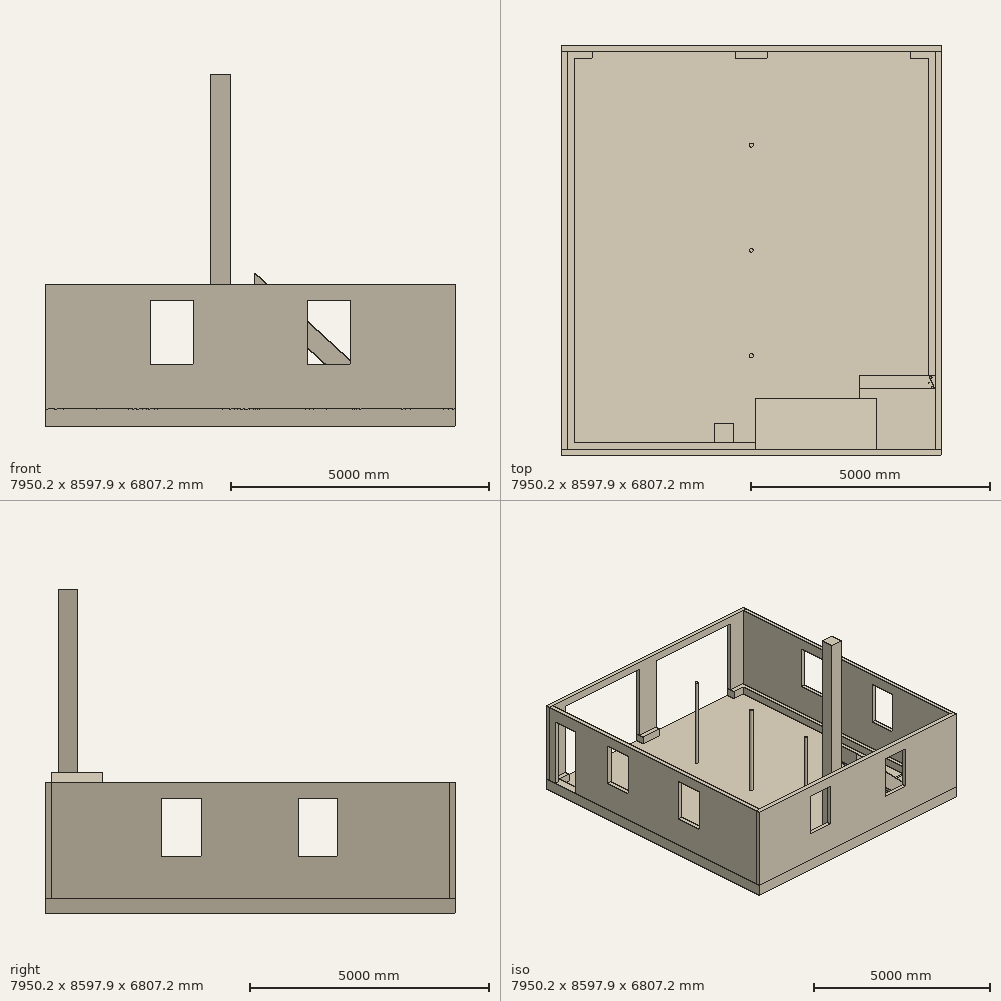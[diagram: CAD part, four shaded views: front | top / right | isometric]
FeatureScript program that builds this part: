
annotation { "Feature Type Name" : "Feature", "Feature Type Description" : "" }
export const myFeature = defineFeature(function(context is Context, id is Id, definition is map)
    precondition{}
    {
        {
            var Q0;
            Q0=qCreatedBy(makeId("Top.planeOp"),FACE);
            var sketch = newSketch(context, id + "F0", { "sketchPlane" : qUnion([Q0])});
            skLineSegment(sketch, "E0.rect.bottom", {"start": v(3975.1, 4298.95) * mm, "end": v(-3975.1, 4298.95) * mm});
            skLineSegment(sketch, "E0.rect.top", {"start": v(3975.1, -4298.95) * mm, "end": v(-3975.1, -4298.95) * mm});
            skLineSegment(sketch, "E0.rect.left", {"start": v(3975.1, 4298.95) * mm, "end": v(3975.1, -4298.95) * mm});
            skLineSegment(sketch, "E0.rect.right", {"start": v(-3975.1, 4298.95) * mm, "end": v(-3975.1, -4298.95) * mm});
            skPoint(sketch, "E0.rect.middle", {"position": v(0, 0) * mm});
            skSolve(sketch);
        }
        {
            var Q0;
            Q0 = qSketchRegion(id + "F0", true);
            extrude(context, id + "F1", {"entities" : qUnion([Q0]), "oppositeDirection" : true, "depth" : 101.6 * mm});
        }
        {
            var Q0;
            Q0=makeQuery(id+"F1.opExtrude","CAP_FACE",FACE,{"disambiguationData":[OSD([sQuery(id+"F0.wireOp",EDGE,"E0.rect.bottom"),sQuery(id+"F0.wireOp",EDGE,"E0.rect.top"),sQuery(id+"F0.wireOp",EDGE,"E0.rect.left"),sQuery(id+"F0.wireOp",EDGE,"E0.rect.right")])],"isStart":true});
            var sketch = newSketch(context, id + "F2", { "sketchPlane" : qUnion([Q0])});
            skLineSegment(sketch, "E1", {"start": v(-3327.4, 4298.95) * mm, "end": v(-3975.1, 4298.95) * mm});
            skLineSegment(sketch, "E2", {"start": v(-3975.1, 4298.95) * mm, "end": v(-3975.1, -4298.95) * mm});
            skLineSegment(sketch, "E3", {"start": v(-3975.1, -4298.95) * mm, "end": v(3975.1, -4298.95) * mm});
            skLineSegment(sketch, "E4", {"start": v(3975.1, -4298.95) * mm, "end": v(3975.1, 4298.95) * mm});
            skLineSegment(sketch, "E5", {"start": v(3975.1, 4298.95) * mm, "end": v(3327.4, 4298.95) * mm});
            skLineSegment(sketch, "E6.0", {"start": v(3708.4, 4032.25) * mm, "end": v(3327.4, 4032.25) * mm});
            skLineSegment(sketch, "E6.1", {"start": v(-3327.4, 4032.25) * mm, "end": v(-3708.4, 4032.25) * mm});
            skLineSegment(sketch, "E6.2", {"start": v(-3708.4, 4032.25) * mm, "end": v(-3708.4, -4032.25) * mm});
            skLineSegment(sketch, "E6.3", {"start": v(-3708.4, -4032.25) * mm, "end": v(3708.4, -4032.25) * mm});
            skLineSegment(sketch, "E6.4", {"start": v(3708.4, -4032.25) * mm, "end": v(3708.4, 4032.25) * mm});
            skLineSegment(sketch, "E7", {"start": v(-3327.4, 4298.95) * mm, "end": v(-3327.4, 4032.25) * mm});
            skLineSegment(sketch, "E8", {"start": v(-330.2, 4298.95) * mm, "end": v(-330.2, 4032.25) * mm});
            skLineSegment(sketch, "E9", {"start": v(-330.2, 4032.25) * mm, "end": v(330.2, 4032.25) * mm});
            skLineSegment(sketch, "E10", {"start": v(330.2, 4032.25) * mm, "end": v(330.2, 4298.95) * mm});
            skLineSegment(sketch, "E11", {"start": v(330.2, 4298.95) * mm, "end": v(-330.2, 4298.95) * mm});
            skLineSegment(sketch, "E12", {"start": v(-330.2, 4032.25) * mm, "end": v(-3327.4, 4032.25) * mm, "construction": true});
            skLineSegment(sketch, "E13", {"start": v(330.2, 4032.25) * mm, "end": v(3327.4, 4032.25) * mm, "construction": true});
            skLineSegment(sketch, "E14", {"start": v(3327.4, 4032.25) * mm, "end": v(3327.4, 4298.95) * mm});
            skSolve(sketch);
        }
        {
            var Q0;
            Q0 = qSketchRegion(id + "F2", true);
            extrude(context, id + "F3", {"entities" : qUnion([Q0]), "operationType" : NewBodyOperationType.ADD, "depth" : 228.6 * mm});
        }
        {
            var Q0;
            Q0=makeQuery(id+"F3.boolean.opBoolean","MERGE",FACE,{"derivedFrom":[makeQuery(id+"F1.opExtrude","SWEPT_FACE",FACE,{"disambiguationData":[OSD([sQuery(id+"F0.wireOp",EDGE,"E0.rect.bottom")])]}),makeQuery(id+"F3.opExtrude","SWEPT_FACE",FACE,{"disambiguationData":[OSD([sQuery(id+"F2.wireOp",EDGE,"E1")])]}),makeQuery(id+"F3.opExtrude","SWEPT_FACE",FACE,{"disambiguationData":[OSD([sQuery(id+"F2.wireOp",EDGE,"E5")])]}),makeQuery(id+"F3.opExtrude","SWEPT_FACE",FACE,{"disambiguationData":[OSD([sQuery(id+"F2.wireOp",EDGE,"E11")])]})]});
            var sketch = newSketch(context, id + "F4", { "sketchPlane" : qUnion([Q0])});
            skLineSegment(sketch, "E15", {"start": v(-3975.1, 228.6) * mm, "end": v(-3975.1, 2641.6) * mm});
            skLineSegment(sketch, "E16", {"start": v(-3975.1, 2641.6) * mm, "end": v(3975.1, 2641.6) * mm});
            skLineSegment(sketch, "E17", {"start": v(3975.1, 2641.6) * mm, "end": v(3975.1, 228.6) * mm});
            skLineSegment(sketch, "E18", {"start": v(3975.1, 228.6) * mm, "end": v(3327.4, 228.6) * mm});
            skLineSegment(sketch, "E19", {"start": v(3327.4, 228.6) * mm, "end": v(3327.4, 2413) * mm});
            skLineSegment(sketch, "E20", {"start": v(3327.4, 2413) * mm, "end": v(330.2, 2413) * mm});
            skLineSegment(sketch, "E21", {"start": v(330.2, 2413) * mm, "end": v(330.2, 228.6) * mm});
            skLineSegment(sketch, "E22", {"start": v(330.2, 228.6) * mm, "end": v(-330.2, 228.6) * mm});
            skLineSegment(sketch, "E23", {"start": v(-330.2, 228.6) * mm, "end": v(-330.2, 2413) * mm});
            skLineSegment(sketch, "E24", {"start": v(-330.2, 2413) * mm, "end": v(-3327.4, 2413) * mm});
            skLineSegment(sketch, "E25", {"start": v(-3327.4, 2413) * mm, "end": v(-3327.4, 228.6) * mm});
            skLineSegment(sketch, "E26", {"start": v(-3327.4, 228.6) * mm, "end": v(-3975.1, 228.6) * mm});
            skSolve(sketch);
        }
        {
            var Q0;
            Q0=makeQuery(id+"F4.imprint","IMPRINT",FACE,{"disambiguationData":[TD([[makeQuery(id+"F4.imprint","IMPRINT",EDGE,{"derivedFrom":sQuery(id+"F4.wireOp",EDGE,"E15")}),-1.0]])]});
            extrude(context, id + "F5", {"entities" : qUnion([Q0]), "oppositeDirection" : true, "depth" : 127 * mm});
        }
        {
            var Q0;
            Q0=makeQuery(id+"F3.boolean.opBoolean","MERGE",FACE,{"derivedFrom":[makeQuery(id+"F1.opExtrude","SWEPT_FACE",FACE,{"disambiguationData":[OSD([sQuery(id+"F0.wireOp",EDGE,"E0.rect.top")])]}),makeQuery(id+"F3.opExtrude","SWEPT_FACE",FACE,{"disambiguationData":[OSD([sQuery(id+"F2.wireOp",EDGE,"E3")])]})]});
            var sketch = newSketch(context, id + "F6", { "sketchPlane" : qUnion([Q0])});
            skLineSegment(sketch, "E27.bottom", {"start": v(-3975.1, 228.6) * mm, "end": v(3975.1, 228.6) * mm});
            skLineSegment(sketch, "E27.top", {"start": v(-3975.1, 2641.6) * mm, "end": v(3975.1, 2641.6) * mm});
            skLineSegment(sketch, "E27.left", {"start": v(-3975.1, 228.6) * mm, "end": v(-3975.1, 2641.6) * mm});
            skLineSegment(sketch, "E27.right", {"start": v(3975.1, 228.6) * mm, "end": v(3975.1, 2641.6) * mm});
            skLineSegment(sketch, "E28.bottom", {"start": v(-1930.4, 2324.1) * mm, "end": v(-1104.9, 2324.1) * mm});
            skLineSegment(sketch, "E28.top", {"start": v(-1930.4, 1092.2) * mm, "end": v(-1104.9, 1092.2) * mm});
            skLineSegment(sketch, "E28.left", {"start": v(-1930.4, 2324.1) * mm, "end": v(-1930.4, 1092.2) * mm});
            skLineSegment(sketch, "E28.right", {"start": v(-1104.9, 2324.1) * mm, "end": v(-1104.9, 1092.2) * mm});
            skLineSegment(sketch, "E29.bottom", {"start": v(1104.9, 2324.1) * mm, "end": v(1930.4, 2324.1) * mm});
            skLineSegment(sketch, "E29.top", {"start": v(1104.9, 1092.2) * mm, "end": v(1930.4, 1092.2) * mm});
            skLineSegment(sketch, "E29.left", {"start": v(1104.9, 2324.1) * mm, "end": v(1104.9, 1092.2) * mm});
            skLineSegment(sketch, "E29.right", {"start": v(1930.4, 2324.1) * mm, "end": v(1930.4, 1092.2) * mm});
            skLineSegment(sketch, "E30", {"start": v(0, 2641.6) * mm, "end": v(0, 228.6) * mm, "construction": true});
            skSolve(sketch);
        }
        {
            var Q0;
            Q0 = qSketchRegion(id + "F6", true);
            extrude(context, id + "F7", {"entities" : qUnion([Q0]), "oppositeDirection" : true, "depth" : 127 * mm});
        }
        {
            var Q0;
            Q0=makeQuery(id+"F3.boolean.opBoolean","MERGE",FACE,{"derivedFrom":[makeQuery(id+"F1.opExtrude","SWEPT_FACE",FACE,{"disambiguationData":[OSD([sQuery(id+"F0.wireOp",EDGE,"E0.rect.right")])]}),makeQuery(id+"F3.opExtrude","SWEPT_FACE",FACE,{"disambiguationData":[OSD([sQuery(id+"F2.wireOp",EDGE,"E2")])]})]});
            var sketch = newSketch(context, id + "F8", { "sketchPlane" : qUnion([Q0])});
            skLineSegment(sketch, "E31.top", {"start": v(-4171.95, 2641.6) * mm, "end": v(4171.95, 2641.6) * mm});
            skLineSegment(sketch, "E31.left", {"start": v(-4171.95, 228.6) * mm, "end": v(-4171.95, 2641.6) * mm});
            skLineSegment(sketch, "E31.right", {"start": v(4171.95, 228.6) * mm, "end": v(4171.95, 2641.6) * mm});
            skLineSegment(sketch, "E32", {"start": v(-4171.95, 228.6) * mm, "end": v(-3930.65, 228.6) * mm});
            skLineSegment(sketch, "E33", {"start": v(-3930.65, 228.6) * mm, "end": v(-3930.65, 2260.6) * mm});
            skLineSegment(sketch, "E34", {"start": v(-3930.65, 2260.6) * mm, "end": v(-3117.85, 2260.6) * mm});
            skLineSegment(sketch, "E35", {"start": v(-3117.85, 2260.6) * mm, "end": v(-3117.85, 228.6) * mm});
            skLineSegment(sketch, "E36", {"start": v(-3117.85, 228.6) * mm, "end": v(4171.95, 228.6) * mm});
            skLineSegment(sketch, "E37.bottom", {"start": v(-1822.45, 2324.1) * mm, "end": v(-996.95, 2324.1) * mm});
            skLineSegment(sketch, "E37.top", {"start": v(-1822.45, 1092.2) * mm, "end": v(-996.95, 1092.2) * mm});
            skLineSegment(sketch, "E37.left", {"start": v(-1822.45, 2324.1) * mm, "end": v(-1822.45, 1092.2) * mm});
            skLineSegment(sketch, "E37.right", {"start": v(-996.95, 2324.1) * mm, "end": v(-996.95, 1092.2) * mm});
            skLineSegment(sketch, "E38.bottom", {"start": v(1035.05, 2324.1) * mm, "end": v(1860.55, 2324.1) * mm});
            skLineSegment(sketch, "E38.top", {"start": v(1035.05, 1092.2) * mm, "end": v(1860.55, 1092.2) * mm});
            skLineSegment(sketch, "E38.left", {"start": v(1035.05, 2324.1) * mm, "end": v(1035.05, 1092.2) * mm});
            skLineSegment(sketch, "E38.right", {"start": v(1860.55, 2324.1) * mm, "end": v(1860.55, 1092.2) * mm});
            skSolve(sketch);
        }
        {
            var Q0;
            Q0=makeQuery(id+"F8.imprint","IMPRINT",FACE,{"disambiguationData":[TD([[makeQuery(id+"F8.imprint","IMPRINT",EDGE,{"derivedFrom":sQuery(id+"F8.wireOp",EDGE,"E31.bottom")}),1.0]])]});
            var Q1;
            Q1=makeQuery(id+"F8.imprint","IMPRINT",FACE,{"disambiguationData":[TD([[makeQuery(id+"F8.imprint","IMPRINT",EDGE,{"derivedFrom":sQuery(id+"F8.wireOp",EDGE,"E31.top")}),-1.0]])]});
            extrude(context, id + "F9", {"entities" : qUnion([Q0, Q1]), "oppositeDirection" : true, "depth" : 127 * mm});
        }
        {
            var Q0;
            Q0=makeQuery(id+"F3.boolean.opBoolean","MERGE",FACE,{"derivedFrom":[makeQuery(id+"F1.opExtrude","SWEPT_FACE",FACE,{"disambiguationData":[OSD([sQuery(id+"F0.wireOp",EDGE,"E0.rect.left")])]}),makeQuery(id+"F3.opExtrude","SWEPT_FACE",FACE,{"disambiguationData":[OSD([sQuery(id+"F2.wireOp",EDGE,"E4")])]})]});
            var sketch = newSketch(context, id + "F10", { "sketchPlane" : qUnion([Q0])});
            skLineSegment(sketch, "E39.bottom", {"start": v(-4171.95, 228.6) * mm, "end": v(4171.95, 228.6) * mm});
            skLineSegment(sketch, "E39.top", {"start": v(-4171.95, 2641.6) * mm, "end": v(4171.95, 2641.6) * mm});
            skLineSegment(sketch, "E39.left", {"start": v(-4171.95, 228.6) * mm, "end": v(-4171.95, 2641.6) * mm});
            skLineSegment(sketch, "E39.right", {"start": v(4171.95, 228.6) * mm, "end": v(4171.95, 2641.6) * mm});
            skSolve(sketch);
        }
        {
            var Q0;
            Q0 = qSketchRegion(id + "F10", true);
            extrude(context, id + "F11", {"entities" : qUnion([Q0]), "oppositeDirection" : true, "depth" : 127 * mm});
        }
        {
            var Q0;
            Q0=makeQuery(id+"F8.imprint","IMPRINT",FACE,{"disambiguationData":[TD([[makeQuery(id+"F8.imprint","IMPRINT",EDGE,{"derivedFrom":sQuery(id+"F8.wireOp",EDGE,"E37.bottom")}),-1.0]])]});
            var Q1;
            Q1=makeQuery(id+"F8.imprint","IMPRINT",FACE,{"disambiguationData":[TD([[makeQuery(id+"F8.imprint","IMPRINT",EDGE,{"derivedFrom":sQuery(id+"F8.wireOp",EDGE,"E38.bottom")}),-1.0]])]});
            var Q2;
            Q2=makeQuery(id+"F11.opExtrude","CAP_FACE",FACE,{"disambiguationData":[OSD([sQuery(id+"F10.wireOp",EDGE,"E39.bottom"),sQuery(id+"F10.wireOp",EDGE,"E39.top"),sQuery(id+"F10.wireOp",EDGE,"E39.left"),sQuery(id+"F10.wireOp",EDGE,"E39.right")])],"isStart":true});
            extrude(context, id + "F12", {"entities" : qUnion([Q0, Q1]), "operationType" : NewBodyOperationType.REMOVE, "endBound" : BoundingType.UP_TO_SURFACE, "oppositeDirection" : true, "endBoundEntityFace" : qUnion([Q2]), "depth" : 25.4 * mm});
        }
        {
            var Q0;
            Q0=makeQuery(id+"F1.opExtrude","CAP_FACE",FACE,{"disambiguationData":[OSD([sQuery(id+"F0.wireOp",EDGE,"E0.rect.bottom"),sQuery(id+"F0.wireOp",EDGE,"E0.rect.top"),sQuery(id+"F0.wireOp",EDGE,"E0.rect.left"),sQuery(id+"F0.wireOp",EDGE,"E0.rect.right")])],"isStart":true});
            var sketch = newSketch(context, id + "F13", { "sketchPlane" : qUnion([Q0])});
            skLineSegment(sketch, "E40.bottom", {"start": v(-381, -4019.55) * mm, "end": v(-774.7, -4019.55) * mm});
            skLineSegment(sketch, "E40.top", {"start": v(-381, -3625.85) * mm, "end": v(-774.7, -3625.85) * mm});
            skLineSegment(sketch, "E40.left", {"start": v(-381, -4019.55) * mm, "end": v(-381, -3625.85) * mm});
            skLineSegment(sketch, "E40.right", {"start": v(-774.7, -4019.55) * mm, "end": v(-774.7, -3625.85) * mm});
            skSolve(sketch);
        }
        {
            var Q0;
            Q0 = qSketchRegion(id + "F13", true);
            extrude(context, id + "F14", {"entities" : qUnion([Q0]), "depth" : 6705.6 * mm});
        }
        {
            var Q0;
            Q0=makeQuery(id+"F1.opExtrude","CAP_FACE",FACE,{"disambiguationData":[OSD([sQuery(id+"F0.wireOp",EDGE,"E0.rect.bottom"),sQuery(id+"F0.wireOp",EDGE,"E0.rect.top"),sQuery(id+"F0.wireOp",EDGE,"E0.rect.left"),sQuery(id+"F0.wireOp",EDGE,"E0.rect.right")])],"isStart":true});
            var sketch = newSketch(context, id + "F15", { "sketchPlane" : qUnion([Q0])});
            skLineSegment(sketch, "E41.bottom", {"start": v(3848.1, -4171.95) * mm, "end": v(2260.6, -4171.95) * mm});
            skLineSegment(sketch, "E41.top", {"start": v(3848.1, -2622.55) * mm, "end": v(2260.6, -2622.55) * mm});
            skLineSegment(sketch, "E41.left", {"start": v(3848.1, -4171.95) * mm, "end": v(3848.1, -2622.55) * mm});
            skLineSegment(sketch, "E41.right", {"start": v(2260.6, -4171.95) * mm, "end": v(2260.6, -2622.55) * mm});
            skSolve(sketch);
        }
        {
            var Q0;
            {var subQ0=sQuery(id+"F15.wireOp",EDGE,"E41.right");var subQ1=sQuery(id+"F15.wireOp",EDGE,"E41.top");var subQ2=makeQuery(id+"F15.imprint","INTERSECT",VERTEX,{"derivedFrom":[subQ1,subQ0]});Q0=makeQuery(id+"F15.imprint","IMPRINT",FACE,{"disambiguationData":[TD([[makeQuery(id+"F15.imprint","IMPRINT",EDGE,{"disambiguationData":[TD([[subQ2,1.0]])],"derivedFrom":subQ1}),1.0]])]});}
            var Q1;
            {var subQ2=sQuery(id+"F15.wireOp",EDGE,"E41.bottom");Q1=makeQuery(id+"F15.imprint","IMPRINT",FACE,{"disambiguationData":[TD([[makeQuery(id+"F15.imprint","IMPRINT",EDGE,{"derivedFrom":subQ2}),-1.0]])]});}
            extrude(context, id + "F16", {"entities" : qUnion([Q0, Q1]), "depth" : 355.6 * mm});
        }
        {
            var Q0;
            Q0=makeQuery(id+"F16.opExtrude","CAP_FACE",FACE,{"disambiguationData":[OSD([sQuery(id+"F15.wireOp",EDGE,"E41.bottom"),sQuery(id+"F15.wireOp",EDGE,"E41.top"),sQuery(id+"F15.wireOp",EDGE,"E41.left"),sQuery(id+"F15.wireOp",EDGE,"E41.right")])],"isStart":false});
            var sketch = newSketch(context, id + "F17", { "sketchPlane" : qUnion([Q0])});
            skLineSegment(sketch, "E42.bottom", {"start": v(2260.6, -2622.55) * mm, "end": v(3848.1, -2622.55) * mm});
            skLineSegment(sketch, "E42.top", {"start": v(2260.6, -2901.95) * mm, "end": v(3848.1, -2901.95) * mm});
            skLineSegment(sketch, "E42.left", {"start": v(2260.6, -2622.55) * mm, "end": v(2260.6, -2901.95) * mm});
            skLineSegment(sketch, "E42.right", {"start": v(3848.1, -2622.55) * mm, "end": v(3848.1, -2901.95) * mm});
            skSolve(sketch);
        }
        {
            var Q0;
            Q0 = qSketchRegion(id + "F17", true);
            extrude(context, id + "F18", {"entities" : qUnion([Q0]), "operationType" : NewBodyOperationType.REMOVE, "oppositeDirection" : true, "depth" : 177.8 * mm});
        }
        {
            var Q0;
            Q0=makeQuery(id+"F7.opExtrude","CAP_FACE",FACE,{"disambiguationData":[OSD([sQuery(id+"F6.wireOp",EDGE,"E27.bottom"),sQuery(id+"F6.wireOp",EDGE,"E27.top"),sQuery(id+"F6.wireOp",EDGE,"E27.left"),sQuery(id+"F6.wireOp",EDGE,"E27.right")])],"isStart":false});
            var sketch = newSketch(context, id + "F19", { "sketchPlane" : qUnion([Q0])});
            skLineSegment(sketch, "E43", {"start": v(-2260.6, 355.6) * mm, "end": v(-76.2, 2355.25) * mm});
            skLineSegment(sketch, "E44", {"start": v(-76.2, 2870.2) * mm, "end": v(-2628.9, 533.4) * mm});
            skLineSegment(sketch, "E45", {"start": v(-2628.9, 533.4) * mm, "end": v(-2628.9, 355.6) * mm});
            skLineSegment(sketch, "E46", {"start": v(-2628.9, 355.6) * mm, "end": v(-2260.6, 355.6) * mm});
            skPoint(sketch, "E47", {"position": v(0, 2641.6) * mm});
            skLineSegment(sketch, "E48", {"start": v(-76.2, 2870.2) * mm, "end": v(-76.2, 2355.25) * mm});
            skSolve(sketch);
        }
        {
            var Q0;
            Q0 = qSketchRegion(id + "F19", true);
            extrude(context, id + "F20", {"entities" : qUnion([Q0]), "operationType" : NewBodyOperationType.ADD, "depth" : 1066.8 * mm});
        }
        {
            var Q0;
            Q0=makeQuery(id+"F1.opExtrude","CAP_FACE",FACE,{"disambiguationData":[OSD([sQuery(id+"F0.wireOp",EDGE,"E0.rect.bottom"),sQuery(id+"F0.wireOp",EDGE,"E0.rect.top"),sQuery(id+"F0.wireOp",EDGE,"E0.rect.left"),sQuery(id+"F0.wireOp",EDGE,"E0.rect.right")])],"isStart":true});
            var sketch = newSketch(context, id + "F21", { "sketchPlane" : qUnion([Q0])});
            skCircle(sketch, "E49", {"center": v(0, 2203.45) * mm, "radius": 44.45 * mm});
            skCircle(sketch, "E50", {"center": v(0, 0) * mm, "radius": 44.45 * mm});
            skCircle(sketch, "E51", {"center": v(0, -2203.45) * mm, "radius": 44.45 * mm});
            skLineSegment(sketch, "E52", {"start": v(0, -2203.45) * mm, "end": v(0, 2203.45) * mm, "construction": true});
            skSolve(sketch);
        }
        {
            var Q0;
            Q0 = qSketchRegion(id + "F21", true);
            var Q1;
            Q1=makeQuery(id+"F5.opExtrude","SWEPT_FACE",FACE,{"disambiguationData":[OSD([sQuery(id+"F4.wireOp",EDGE,"E16")])]});
            extrude(context, id + "F22", {"entities" : qUnion([Q0]), "operationType" : NewBodyOperationType.ADD, "endBound" : BoundingType.UP_TO_SURFACE, "endBoundEntityFace" : qUnion([Q1]), "depth" : 25.4 * mm});
        }
    });
